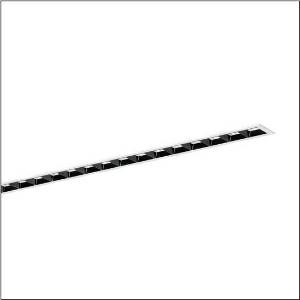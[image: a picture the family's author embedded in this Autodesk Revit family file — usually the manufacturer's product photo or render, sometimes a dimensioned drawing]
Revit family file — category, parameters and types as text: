
# Revit family: silica_r__21_51mx11tctaw_2435
name_source: partatom
category: Lighting Fixtures
units: mm (PartAtom-declared; Revit-internal decimal feet)

## family parameters
Cut with Voids When Loaded = No
Host = Face
Light Source = No
Part Type = Normal
Room Calculation Point = No
Round Connector Dimension = Use Diameter
Shared = No

## types (1)
- --- (1 x LED, 9300 lm, 80.5 W, 6500K)
    Apparent Load = 81 VA
    CIE Flux Codes = 85 99 100 100 100
    Color Rendering = 80
    Color Temperature = 6500K
    Default Elevation = 1800 mm
    Description = Silica® 21, office luminaire, primary light control with darklight reflector, of PMMA, black, CAT 2 (L<= 3000cd/m²), light emission: direct distribution, primary light characteristic: symmetric, installation type: recessed, LED, rated luminous flux: 9.300lm, luminous efficacy: 110lm/W, light colour: 8tw, colour temperature: 2700..6500K, control gear: DALI DT8, with terminal, 3+2-pole, max. 2.5mm², mains connection: 220..240V, AC, 50/60Hz, rated input power: 84.6W, luminaire housing, of aluminium, traffic white (RAL 9016), length: 3.028mm, width: 79mm, height: 53mm, protection rating (complete): IP20, insulation class (complete): insulation class I (protective earthing), certification: CE, ENEC, VDE, permissible operating ambient temperature: 0..+35°C, standard: EN 50419, packaging unit: 1 piece
    Height = 0 mm  [stored 0 ft]
    Lamp = 1 x LED
    Lamp Light Flux = 9300 lm
    Lamp Power = 80.5 W
    Lamp count = 1
    Length = 3027 mm
    Luminous efficacy = 116 lm/W
    Manufacturer = Siteco
    ModVariant = No
    Model = 51MX11TCTAW
    Mounting Place = Ceiling
    Mounting Type = Recessed
    Number of Poles = 1
    OnlyDefault = Yes
    Power Factor = 1
    Product Name = Silica® 21
    Product group = office luminaire | ceiling recessed
    ProductGroupID = 401
    Protection Class = Protection class I
    Protection Degree = IP 20
    RLX_Detail_Level = 1
    RLX_Emergency_Light_Flux = 0 lm
    RLX_Emergency_Type = 0
    RLX_Emergency_Type_DB = No
    RlxData = <blob elided: 59373 chars, md5=dc84527e>
    Socket = socket
    Standby Power = 0 W
    System Light Flux = 9300 lm
    System Power = 81 W
    Type Comments = individual setting
    Type Image = l_1335880.jpg
    URL = http://relux.com
    VarID = @adj_140094
    Voltage = 0 V
    Weight = 0.00 kg
    Width = 79 mm

note: [stored X ft] marks values corroborated as IEEE doubles in the binary element streams (Revit-internal decimal feet)

## geometry (parser evidence)
native form markers: Blend x4, Sweep x12
no freeform markers — native parametric forms only
